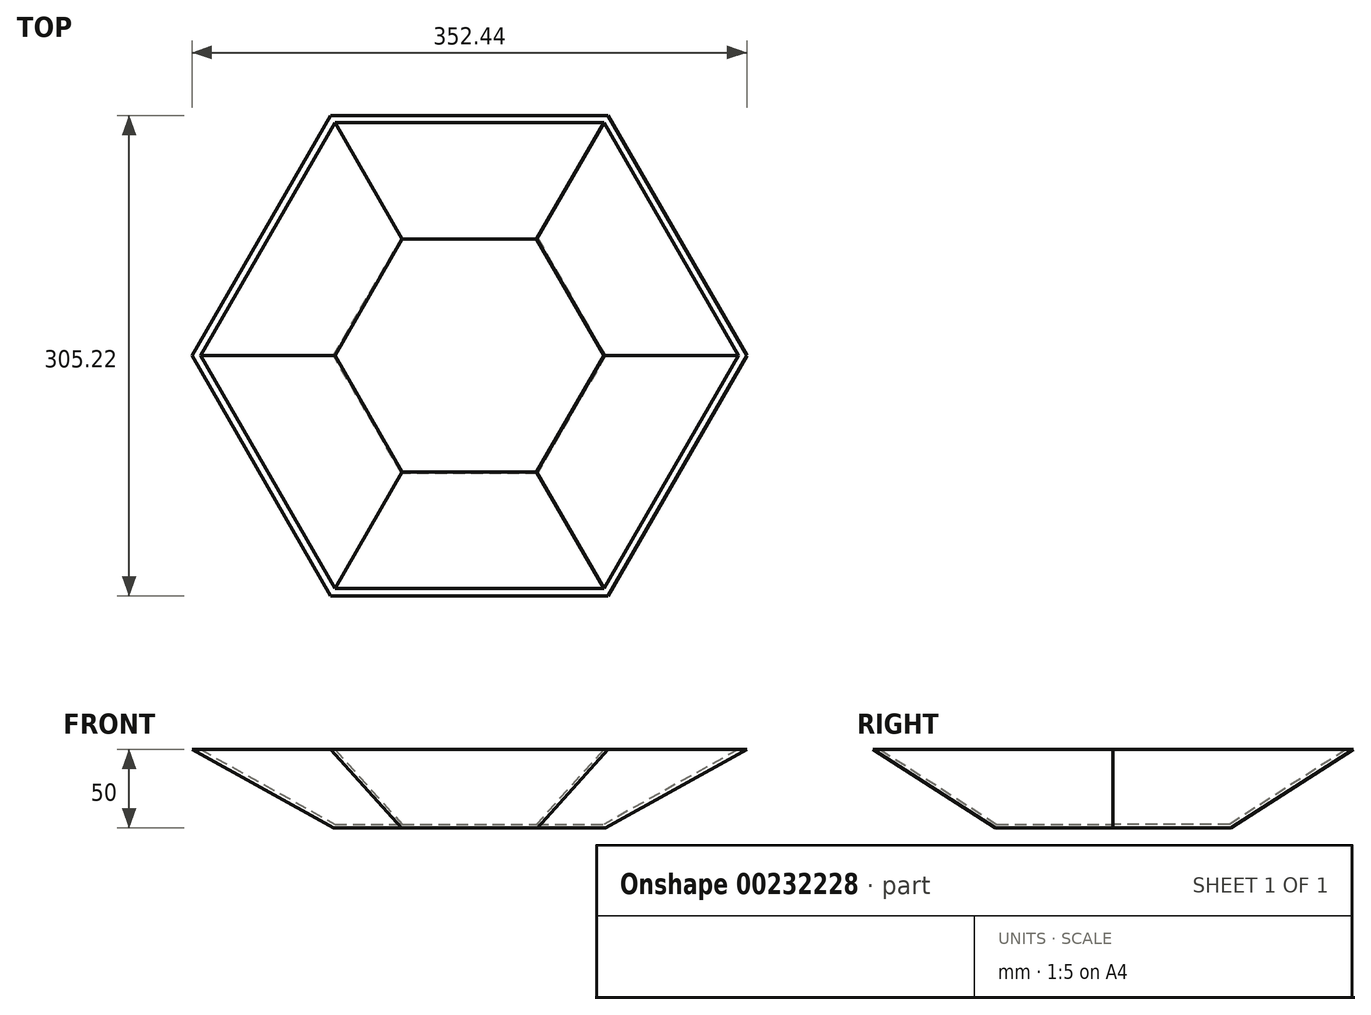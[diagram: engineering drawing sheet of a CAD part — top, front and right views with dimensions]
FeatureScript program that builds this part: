
annotation { "Feature Type Name" : "Feature", "Feature Type Description" : "" }
export const myFeature = defineFeature(function(context is Context, id is Id, definition is map)
    precondition{}
    {
        {
            var Q0;
            Q0=qCreatedBy(makeId("Top.planeOp"),FACE);
            var sketch = newSketch(context, id + "F0", { "sketchPlane" : qUnion([Q0])});
            skCircle(sketch, "E0.cCircle", {"center": v(0, 0) * mm, "radius": 86.3 * mm, "construction": true});
            skLineSegment(sketch, "E0.0", {"start": v(43.15, 74.74) * mm, "end": v(86.3, 0) * mm});
            skLineSegment(sketch, "E0.1", {"start": v(86.3, 0) * mm, "end": v(43.15, -74.74) * mm});
            skLineSegment(sketch, "E0.2", {"start": v(43.15, -74.74) * mm, "end": v(-43.15, -74.74) * mm});
            skLineSegment(sketch, "E0.3", {"start": v(-43.15, -74.74) * mm, "end": v(-86.3, 0) * mm});
            skLineSegment(sketch, "E0.4", {"start": v(-86.3, 0) * mm, "end": v(-43.15, 74.74) * mm});
            skLineSegment(sketch, "E0.5", {"start": v(-43.15, 74.74) * mm, "end": v(43.15, 74.74) * mm});
            skSolve(sketch);
        }
        {
            var Q0;
            Q0=makeQuery(id+"F0.imprint","IMPRINT",FACE,{"disambiguationData":[TD([[makeQuery(id+"F0.imprint","IMPRINT",EDGE,{"derivedFrom":sQuery(id+"F0.wireOp",EDGE,"E0.0")}),-1.0]])]});
            extrude(context, id + "F1", {"entities" : qUnion([Q0]), "depth" : 50 * mm, "hasDraft" : true, "draftAngle" : 1 * radian});
        }
        {
            var Q0;
            Q0=makeQuery(id+"F1.opExtrude","CAP_FACE",FACE,{"disambiguationData":[OSD([sQuery(id+"F0.wireOp",EDGE,"E0.0"),sQuery(id+"F0.wireOp",EDGE,"E0.1"),sQuery(id+"F0.wireOp",EDGE,"E0.2"),sQuery(id+"F0.wireOp",EDGE,"E0.3"),sQuery(id+"F0.wireOp",EDGE,"E0.4"),sQuery(id+"F0.wireOp",EDGE,"E0.5")])],"isStart":false});
            shell(context, id + "F2", {"entities" : qUnion([Q0]), "thickness" : 2.5 * mm});
        }
    });
